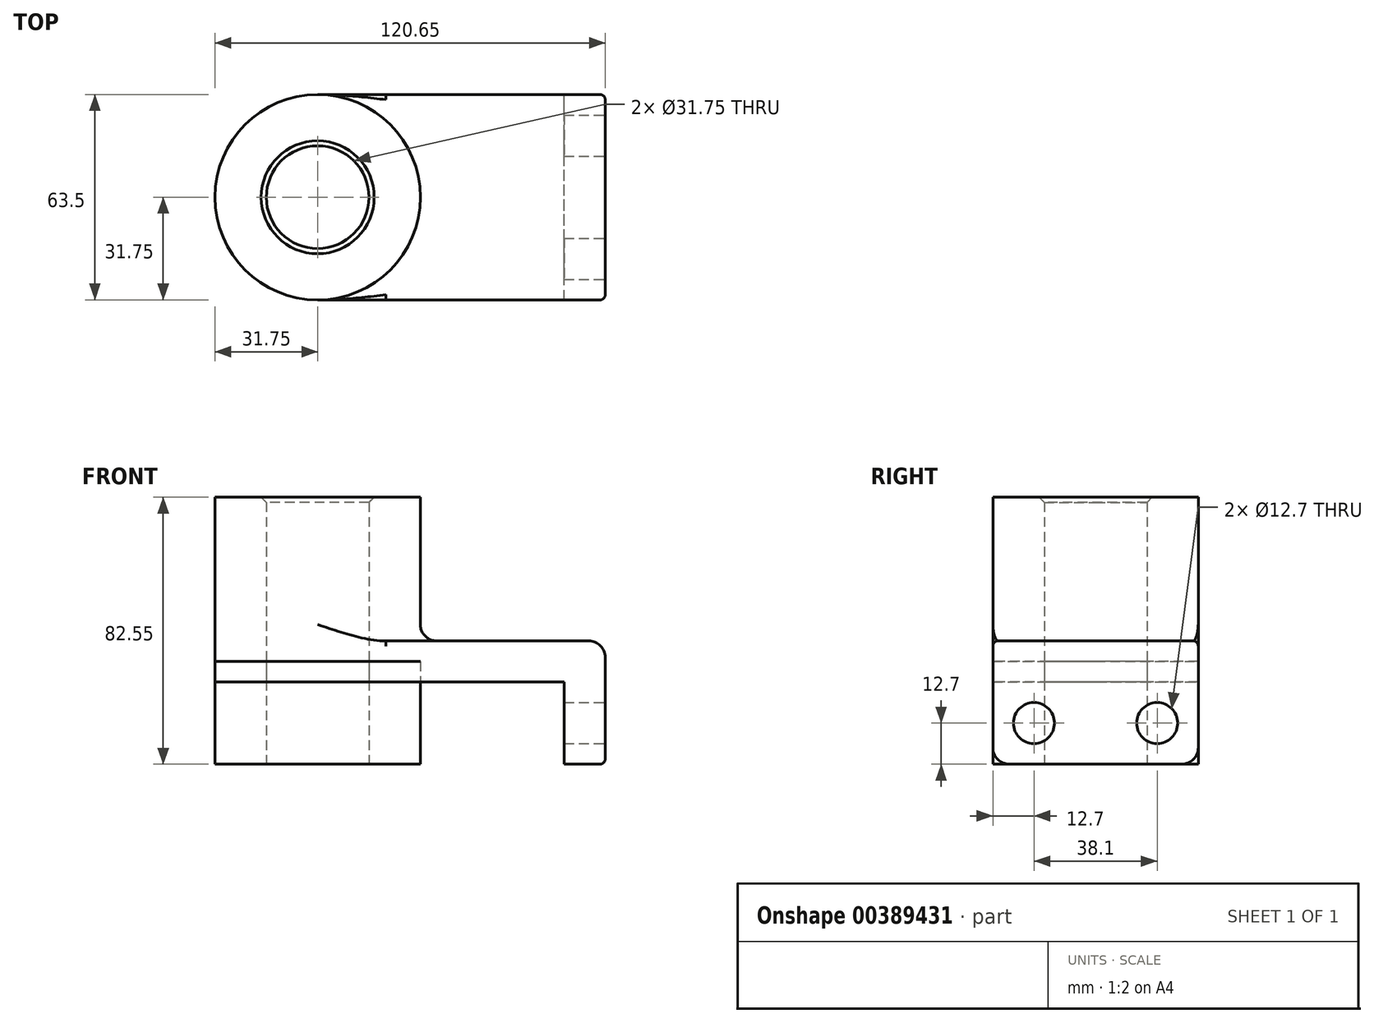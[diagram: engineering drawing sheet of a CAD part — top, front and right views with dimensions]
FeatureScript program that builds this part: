
annotation { "Feature Type Name" : "Feature", "Feature Type Description" : "" }
export const myFeature = defineFeature(function(context is Context, id is Id, definition is map)
    precondition{}
    {
        {
            var Q0;
            Q0=qCreatedBy(makeId("Top.planeOp"),FACE);
            var sketch = newSketch(context, id + "F0", { "sketchPlane" : qUnion([Q0])});
            skLineSegment(sketch, "E0.bottom", {"start": v(44.45, -31.75) * mm, "end": v(-44.45, -31.75) * mm});
            skLineSegment(sketch, "E0.top", {"start": v(44.45, 31.75) * mm, "end": v(-44.45, 31.75) * mm});
            skLineSegment(sketch, "E0.left", {"start": v(44.45, -31.75) * mm, "end": v(44.45, 31.75) * mm});
            skLineSegment(sketch, "E0.right", {"start": v(-44.45, -31.75) * mm, "end": v(-44.45, 31.75) * mm});
            skPoint(sketch, "E0.middle", {"position": v(0, 0) * mm});
            skCircle(sketch, "E1", {"center": v(-44.45, 0) * mm, "radius": 31.75 * mm});
            skCircle(sketch, "E2", {"center": v(-44.45, 0) * mm, "radius": 15.88 * mm});
            skSolve(sketch);
        }
        {
            var Q0;
            {var subQ1=sQuery(id+"F0.wireOp",EDGE,"E0.right");var subQ3=sQuery(id+"F0.wireOp",EDGE,"E2");var subQ4=makeQuery(id+"F0.imprint","INTERSECT",VERTEX,{"disambiguationData":[OD(0.0)],"derivedFrom":[subQ1,subQ3]});Q0=makeQuery(id+"F0.imprint","IMPRINT",FACE,{"disambiguationData":[TD([[makeQuery(id+"F0.imprint","IMPRINT",EDGE,{"disambiguationData":[TD([[subQ4,1.0]])],"derivedFrom":subQ3}),-1.0]])]});}
            var Q1;
            {var subQ1=sQuery(id+"F0.wireOp",EDGE,"E0.right");var subQ3=sQuery(id+"F0.wireOp",EDGE,"E2");var subQ4=makeQuery(id+"F0.imprint","INTERSECT",VERTEX,{"disambiguationData":[OD(0.0)],"derivedFrom":[subQ1,subQ3]});Q1=makeQuery(id+"F0.imprint","IMPRINT",FACE,{"disambiguationData":[TD([[makeQuery(id+"F0.imprint","IMPRINT",EDGE,{"disambiguationData":[TD([[subQ4,-1.0]])],"derivedFrom":subQ3}),-1.0]])]});}
            var Q2;
            {var subQ0=sQuery(id+"F0.wireOp",EDGE,"E0.bottom");Q2=makeQuery(id+"F0.imprint","IMPRINT",FACE,{"disambiguationData":[TD([[makeQuery(id+"F0.imprint","IMPRINT",EDGE,{"derivedFrom":subQ0}),-1.0]])]});}
            extrude(context, id + "F1", {"entities" : qUnion([Q0, Q1, Q2]), "depth" : 12.7 * mm});
        }
        {
            var Q0;
            {var subQ1=sQuery(id+"F0.wireOp",EDGE,"E0.right");var subQ3=sQuery(id+"F0.wireOp",EDGE,"E2");var subQ4=makeQuery(id+"F0.imprint","INTERSECT",VERTEX,{"disambiguationData":[OD(0.0)],"derivedFrom":[subQ1,subQ3]});Q0=makeQuery(id+"F0.imprint","IMPRINT",FACE,{"disambiguationData":[TD([[makeQuery(id+"F0.imprint","IMPRINT",EDGE,{"disambiguationData":[TD([[subQ4,-1.0]])],"derivedFrom":subQ3}),-1.0]])]});}
            var Q1;
            {var subQ1=sQuery(id+"F0.wireOp",EDGE,"E0.right");var subQ3=sQuery(id+"F0.wireOp",EDGE,"E2");var subQ4=makeQuery(id+"F0.imprint","INTERSECT",VERTEX,{"disambiguationData":[OD(0.0)],"derivedFrom":[subQ1,subQ3]});Q1=makeQuery(id+"F0.imprint","IMPRINT",FACE,{"disambiguationData":[TD([[makeQuery(id+"F0.imprint","IMPRINT",EDGE,{"disambiguationData":[TD([[subQ4,1.0]])],"derivedFrom":subQ3}),-1.0]])]});}
            extrude(context, id + "F2", {"entities" : qUnion([Q0, Q1]), "operationType" : NewBodyOperationType.ADD, "depth" : 50.8 * mm});
        }
        {
            var Q0;
            Q0=makeQuery(id+"F1.opExtrude","SWEPT_FACE",FACE,{"disambiguationData":[OSD([sQuery(id+"F0.wireOp",EDGE,"E0.left")])]});
            var sketch = newSketch(context, id + "F3", { "sketchPlane" : qUnion([Q0])});
            skLineSegment(sketch, "E3.bottom", {"start": v(-31.75, 12.7) * mm, "end": v(31.75, 12.7) * mm});
            skLineSegment(sketch, "E3.top", {"start": v(-31.75, -25.4) * mm, "end": v(31.75, -25.4) * mm});
            skLineSegment(sketch, "E3.left", {"start": v(-31.75, 12.7) * mm, "end": v(-31.75, -25.4) * mm});
            skLineSegment(sketch, "E3.right", {"start": v(31.75, 12.7) * mm, "end": v(31.75, -25.4) * mm});
            skCircle(sketch, "E4", {"center": v(-19.05, -12.7) * mm, "radius": 6.35 * mm});
            skLineSegment(sketch, "E5", {"start": v(0, 0) * mm, "end": v(0, -25.4) * mm, "construction": true});
            skPoint(sketch, "E5.endSnap0", {"position": v(0, 0) * mm});
            skCircle(sketch, "E6.MirrorC", {"center": v(19.05, -12.7) * mm, "radius": 6.35 * mm});
            skSolve(sketch);
        }
        {
            var Q0;
            Q0=qSketchRegion(id+"F3",true);
            extrude(context, id + "F4", {"entities" : qUnion([Q0]), "operationType" : NewBodyOperationType.ADD, "oppositeDirection" : true, "depth" : 12.7 * mm});
        }
        {
            var Q0;
            {var subQ0=sQuery(id+"F0.wireOp",EDGE,"E1");Q0=makeQuery(id+"F2.boolean.opBoolean","INTERSECT",EDGE,{"derivedFrom":[makeQuery(id+"F1.opExtrude","CAP_FACE",FACE,{"disambiguationData":[OSD([sQuery(id+"F0.wireOp",EDGE,"E0.bottom"),sQuery(id+"F0.wireOp",EDGE,"E0.top"),sQuery(id+"F0.wireOp",EDGE,"E0.left"),subQ0,sQuery(id+"F0.wireOp",EDGE,"E2")])],"isStart":false}),makeQuery(id+"F2.opExtrude","SWEPT_FACE",FACE,{"disambiguationData":[OSD([subQ0])]})]});}
            var Q1;
            Q1=makeQuery(id+"F4.opExtrude","SWEPT_EDGE",EDGE,{"disambiguationData":[OSD([sQuery(id+"F3.wireOp",EDGE,"E3.top"),sQuery(id+"F3.wireOp",EDGE,"E3.left")])]});
            var Q2;
            Q2=makeQuery(id+"F1.opExtrude","CAP_EDGE",EDGE,{"disambiguationData":[OSD([sQuery(id+"F0.wireOp",EDGE,"E0.left")])],"isStart":false});
            var Q3;
            Q3=makeQuery(id+"F4.opExtrude","SWEPT_EDGE",EDGE,{"disambiguationData":[OSD([sQuery(id+"F3.wireOp",EDGE,"E3.top"),sQuery(id+"F3.wireOp",EDGE,"E3.right")])]});
            fillet(context, id + "F5", {"entities" : qUnion([Q0, Q1, Q2, Q3]), "radius" : 5.08 * mm, "tangentPropagation" : true, "allowEdgeOverflow" : false});
        }
        {
            var Q0;
            Q0=makeQuery(id+"F1.opExtrude","CAP_EDGE",EDGE,{"disambiguationData":[OSD([sQuery(id+"F0.wireOp",EDGE,"E0.bottom")])],"isStart":false});
            fillet(context, id + "F6", {"entities" : qUnion([Q0]), "radius" : 1.59 * mm, "tangentPropagation" : true, "allowEdgeOverflow" : false});
        }
        {
            var Q0;
            {var subQ0=sQuery(id+"F0.wireOp",EDGE,"E2");var subQ1=sQuery(id+"F0.wireOp",EDGE,"E0.right");var subQ2=makeQuery(id+"F0.imprint","INTERSECT",VERTEX,{"disambiguationData":[OD(0.0)],"derivedFrom":[subQ1,subQ0]});Q0=makeQuery(id+"F0.imprint","IMPRINT",FACE,{"disambiguationData":[TD([[makeQuery(id+"F0.imprint","IMPRINT",EDGE,{"disambiguationData":[TD([[subQ2,-1.0]])],"derivedFrom":subQ1}),-1.0]])]});}
            var Q1;
            {var subQ0=sQuery(id+"F0.wireOp",EDGE,"E2");var subQ1=sQuery(id+"F0.wireOp",EDGE,"E0.right");var subQ2=makeQuery(id+"F0.imprint","INTERSECT",VERTEX,{"disambiguationData":[OD(0.0)],"derivedFrom":[subQ1,subQ0]});Q1=makeQuery(id+"F0.imprint","IMPRINT",FACE,{"disambiguationData":[TD([[makeQuery(id+"F0.imprint","IMPRINT",EDGE,{"disambiguationData":[TD([[subQ2,-1.0]])],"derivedFrom":subQ1}),1.0]])]});}
            extrude(context, id + "F7", {"entities" : qUnion([Q0, Q1]), "depth" : 57.15 * mm});
        }
        {
            var Q0;
            Q0=makeQuery(id+"F7.opExtrude","CAP_EDGE",EDGE,{"disambiguationData":[OSD([sQuery(id+"F0.wireOp",EDGE,"E2")])],"isStart":true});
            fillet(context, id + "F8", {"entities" : qUnion([Q0]), "radius" : 1.59 * mm, "tangentPropagation" : true, "allowEdgeOverflow" : false});
        }
        {
            var Q0;
            Q0=makeQuery(id+"F7.opExtrude","CAP_EDGE",EDGE,{"disambiguationData":[OSD([sQuery(id+"F0.wireOp",EDGE,"E2")])],"isStart":false});
            chamfer(context, id + "F9", {"entities" : qUnion([Q0]), "width" : 1.59 * mm, "tangentPropagation" : true});
        }
        {
            var Q0;
            {var subQ0=sQuery(id+"F0.wireOp",EDGE,"E2");var subQ1=sQuery(id+"F0.wireOp",EDGE,"E0.right");var subQ2=makeQuery(id+"F0.imprint","INTERSECT",VERTEX,{"disambiguationData":[OD(0.0)],"derivedFrom":[subQ1,subQ0]});Q0=makeQuery(id+"F0.imprint","IMPRINT",FACE,{"disambiguationData":[TD([[makeQuery(id+"F0.imprint","IMPRINT",EDGE,{"disambiguationData":[TD([[subQ2,-1.0]])],"derivedFrom":subQ1}),1.0]])]});}
            var Q1;
            {var subQ1=sQuery(id+"F0.wireOp",EDGE,"E0.right");var subQ3=sQuery(id+"F0.wireOp",EDGE,"E2");var subQ4=makeQuery(id+"F0.imprint","INTERSECT",VERTEX,{"disambiguationData":[OD(0.0)],"derivedFrom":[subQ1,subQ3]});Q1=makeQuery(id+"F0.imprint","IMPRINT",FACE,{"disambiguationData":[TD([[makeQuery(id+"F0.imprint","IMPRINT",EDGE,{"disambiguationData":[TD([[subQ4,1.0]])],"derivedFrom":subQ3}),-1.0]])]});}
            var Q2;
            {var subQ1=sQuery(id+"F0.wireOp",EDGE,"E0.right");var subQ3=sQuery(id+"F0.wireOp",EDGE,"E2");var subQ4=makeQuery(id+"F0.imprint","INTERSECT",VERTEX,{"disambiguationData":[OD(0.0)],"derivedFrom":[subQ1,subQ3]});Q2=makeQuery(id+"F0.imprint","IMPRINT",FACE,{"disambiguationData":[TD([[makeQuery(id+"F0.imprint","IMPRINT",EDGE,{"disambiguationData":[TD([[subQ4,-1.0]])],"derivedFrom":subQ3}),-1.0]])]});}
            var Q3;
            {var subQ0=sQuery(id+"F0.wireOp",EDGE,"E2");var subQ1=sQuery(id+"F0.wireOp",EDGE,"E0.right");var subQ2=makeQuery(id+"F0.imprint","INTERSECT",VERTEX,{"disambiguationData":[OD(0.0)],"derivedFrom":[subQ1,subQ0]});Q3=makeQuery(id+"F0.imprint","IMPRINT",FACE,{"disambiguationData":[TD([[makeQuery(id+"F0.imprint","IMPRINT",EDGE,{"disambiguationData":[TD([[subQ2,-1.0]])],"derivedFrom":subQ1}),-1.0]])]});}
            extrude(context, id + "F10", {"entities" : qUnion([Q0, Q1, Q2, Q3]), "operationType" : NewBodyOperationType.ADD, "oppositeDirection" : true, "depth" : 25.4 * mm});
        }
        {
            var Q0;
            {var subQ1=sQuery(id+"F0.wireOp",EDGE,"E0.right");var subQ3=sQuery(id+"F0.wireOp",EDGE,"E2");var subQ4=makeQuery(id+"F0.imprint","INTERSECT",VERTEX,{"disambiguationData":[OD(0.0)],"derivedFrom":[subQ1,subQ3]});Q0=makeQuery(id+"F0.imprint","IMPRINT",FACE,{"disambiguationData":[TD([[makeQuery(id+"F0.imprint","IMPRINT",EDGE,{"disambiguationData":[TD([[subQ4,1.0]])],"derivedFrom":subQ3}),-1.0]])]});}
            var Q1;
            {var subQ1=sQuery(id+"F0.wireOp",EDGE,"E0.right");var subQ3=sQuery(id+"F0.wireOp",EDGE,"E2");var subQ4=makeQuery(id+"F0.imprint","INTERSECT",VERTEX,{"disambiguationData":[OD(0.0)],"derivedFrom":[subQ1,subQ3]});Q1=makeQuery(id+"F0.imprint","IMPRINT",FACE,{"disambiguationData":[TD([[makeQuery(id+"F0.imprint","IMPRINT",EDGE,{"disambiguationData":[TD([[subQ4,-1.0]])],"derivedFrom":subQ3}),-1.0]])]});}
            extrude(context, id + "F11", {"entities" : qUnion([Q0, Q1]), "depth" : 6.35 * mm});
        }
    });
